# Revit family: Water_Heater-Racks-02
name_source: partatom
category: Specialty Equipment
revit_build: Autodesk Revit 2016 (Build: 20150220_1215(x64)
units: mm (PartAtom-declared; Revit-internal decimal feet)

## family parameters
Cut with Voids When Loaded = No
Host = Face
OmniClass Number = 23.40.20.27.17
OmniClass Title = Racking
Part Type = Normal
Room Calculation Point = No
Round Connector Dimension = Use Diameter
Shared = No

## types (1)
- Rack Base Component
    Default Elevation = 48 "
    Depth = 23.8 "
    Description = Ready-Link ® Rack Base. The free standing rack system is designed for infield assembly and indoor installation only. Designed to work with NPE, NCB, NFB and NHB series units. Base rack allows installation for up to 2 units back to back.
    Finish = Metal - Navien - Carbon Steel - White
    Height = 65.5 "
    Manufacturer = Navien, Inc.
    Manufacturer Fax Number = (949) 420-0430
    Model = GFFM-KDIZUS
    Product Documentation Link = https://www.navieninc.com
    Product Name = Ready-Link® Rack
    Product Page URL = https://www.navieninc.com
    URL = https://www.navieninc.com
    Version = 2016 - v1.0.a
    Warranty = https://www.navieninc.com
    Width = 22.3 "
    o/c Between Racks = 20 "

## geometry (parser evidence)
native form markers: Sweep x2
no freeform markers — native parametric forms only
